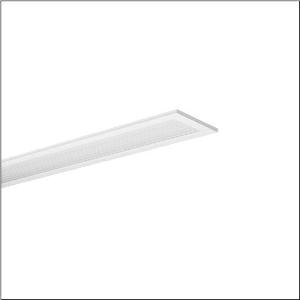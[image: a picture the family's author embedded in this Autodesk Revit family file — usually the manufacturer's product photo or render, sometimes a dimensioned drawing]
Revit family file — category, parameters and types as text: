
# Revit family: apollon_r__21_linear_51mq16wd2414_c89d
name_source: partatom
category: Lighting Fixtures
units: mm (PartAtom-declared; Revit-internal decimal feet)

## family parameters
Cut with Voids When Loaded = No
Host = Face
Light Source = No
Part Type = Normal
Room Calculation Point = No
Round Connector Dimension = Use Diameter
Shared = No

## types (1)
- Apollon® 21 linear (1 x LED, 3400 lm, 23.2 W, 4000K)
    Apparent Load = 23 VA
    CIE Flux Codes = 64 88 97 100 100
    Color Rendering = 80
    Color Temperature = 4000K
    Default Elevation = 1800 mm
    Description = Apollon® 21 linear, office luminaire, primary optical cover: micro prismatic cover, of PMMA, CAT 2 (L<= 3000cd/m²), light emission: direct distribution, primary light characteristic: symmetric, installation type: lay-in mounting, LED, rated luminous flux: 3.400lm, luminous efficacy: 147lm/W, light colour: 840, colour temperature: 4000K, with terminal, 5-pole, mains connection: 220..240V, AC/DC, 0/50..60Hz, rated input power: 23.2W, housing, of aluminium, coated, traffic white (RAL 9016), length: 1.545mm, width: 179mm, height: 30mm, housing upper side, of sheet steel, galvanised, protection rating (complete): IP20, protection rating (lamp compartment, on room side): IP50, insulation class (complete): insulation class II (safety insulation), certification: CE, ENEC, impact resistance: IK03, permissible operating ambient temperature: -20..+45°C, permissible storage temperature: -40..+80°C, packaging unit: 1 piece
    Height = 0 mm  [stored 0 ft]
    Lamp = 1 x LED
    Lamp Light Flux = 3400 lm
    Lamp Power = 23.2 W
    Lamp count = 1
    Length = 1545 mm
    Luminous efficacy = 147 lm/W
    Manufacturer = Siteco
    ModVariant = No
    Model = 51MQ16WD2414
    Mounting Place = Ceiling
    Mounting Type = Recessed
    Number of Poles = 1
    OnlyDefault = Yes
    Power Factor = 1
    Product Name = Apollon® 21 linear
    Product group = office luminaire | ceiling recessed
    ProductGroupID = 401
    Protection Class = Protection class II
    Protection Degree = IP 20
    RLX_Detail_Level = 1
    RLX_Emergency_Light_Flux = 0 lm
    RLX_Emergency_Type = 0
    RLX_Emergency_Type_DB = No
    RlxData = <blob elided: 12549 chars, md5=2975c319>
    Socket = socket
    Standby Power = 0 W
    System Light Flux = 3400 lm
    System Power = 23 W
    Type Comments = Product without accessories
    Type Image = l_1291018.jpg
    URL = http://relux.com
    VarID = ---
    Voltage = 0 V
    Weight = 0.00 kg
    Width = 179 mm

note: [stored X ft] marks values corroborated as IEEE doubles in the binary element streams (Revit-internal decimal feet)

## geometry (parser evidence)
native form markers: Sweep x10
no freeform markers — native parametric forms only
